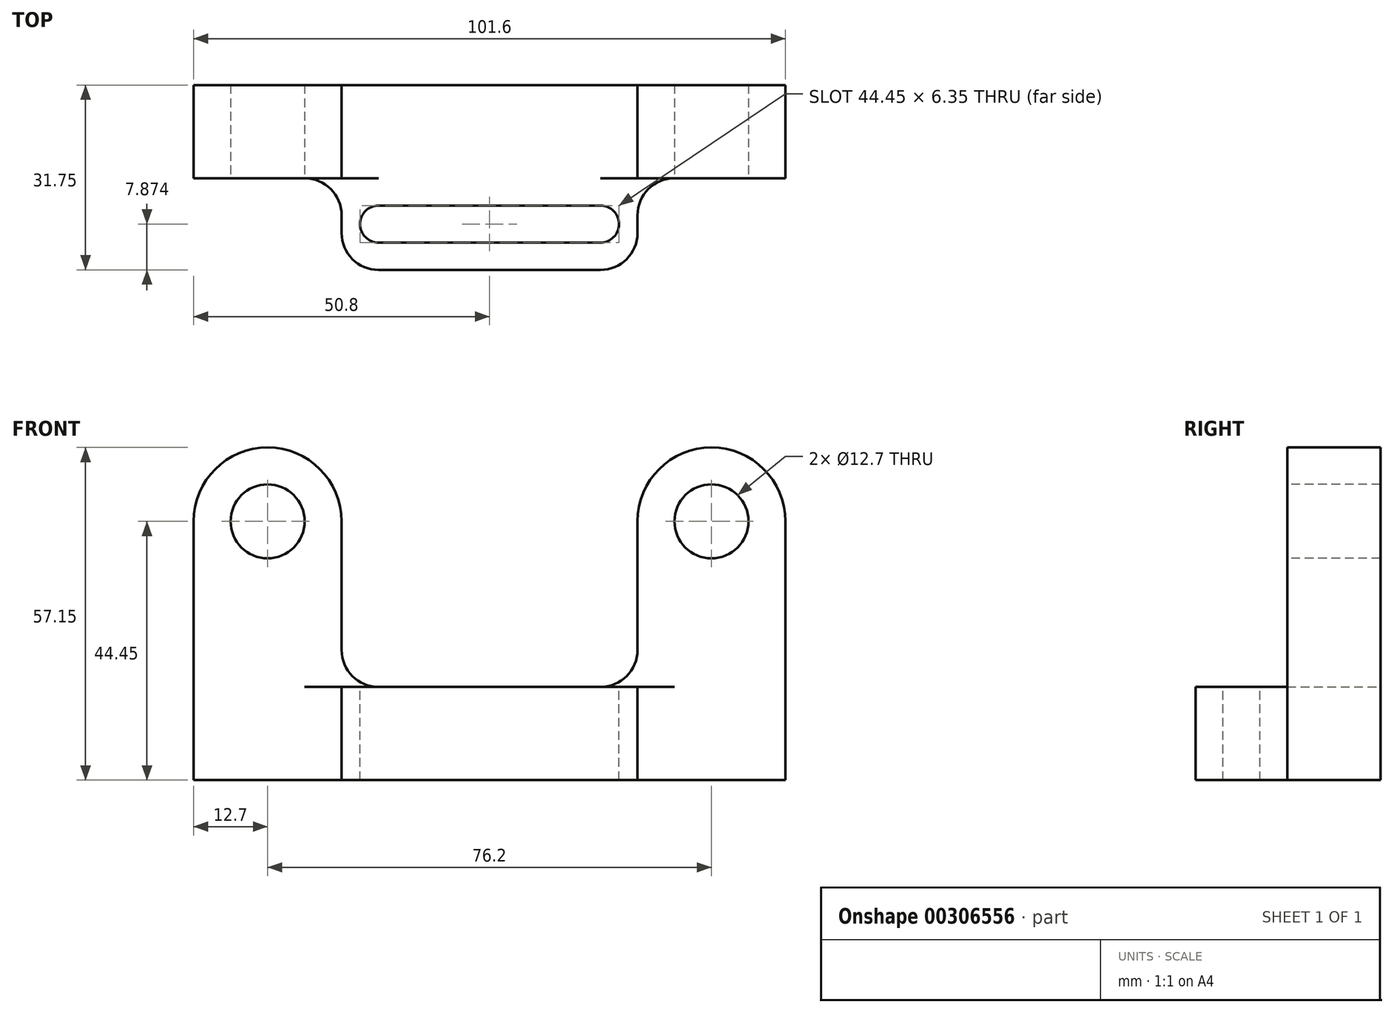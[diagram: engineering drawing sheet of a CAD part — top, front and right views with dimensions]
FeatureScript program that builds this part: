
annotation { "Feature Type Name" : "Feature", "Feature Type Description" : "" }
export const myFeature = defineFeature(function(context is Context, id is Id, definition is map)
    precondition{}
    {
        {
            var Q0;
            Q0=qCreatedBy(makeId("Front.planeOp"),FACE);
            var sketch = newSketch(context, id + "F0", { "sketchPlane" : qUnion([Q0])});
            skLineSegment(sketch, "E0", {"start": v(0, 0) * mm, "end": v(50.8, 0) * mm});
            skLineSegment(sketch, "E1", {"start": v(50.8, 0) * mm, "end": v(50.8, 44.45) * mm});
            skLineSegment(sketch, "E2", {"start": v(0, 0) * mm, "end": v(0, 16) * mm});
            skLineSegment(sketch, "E3", {"start": v(0, 16) * mm, "end": v(19.05, 16) * mm});
            skLineSegment(sketch, "E4", {"start": v(25.4, 22.35) * mm, "end": v(25.4, 44.45) * mm});
            skArc(sketch, "E5", {"start": v(50.8, 44.45) * mm, "mid": v(38.1, 57.15) * mm, "end": v(25.4, 44.45) * mm});
            skPoint(sketch, "E6.visualSharp", {"position": v(25.4, 16) * mm});
            skArc(sketch, "E6.filletArc", {"start": v(19.05, 16) * mm, "mid": v(23.54, 17.86) * mm, "end": v(25.4, 22.35) * mm});
            skLineSegment(sketch, "E7", {"start": v(0, 16) * mm, "end": v(-19.05, 16) * mm});
            skLineSegment(sketch, "E8", {"start": v(-25.4, 22.35) * mm, "end": v(-25.4, 44.45) * mm});
            skLineSegment(sketch, "E9", {"start": v(-50.8, 44.45) * mm, "end": v(-50.8, 0) * mm});
            skLineSegment(sketch, "E10", {"start": v(-50.8, 0) * mm, "end": v(0, 0) * mm});
            skArc(sketch, "E11", {"start": v(-25.4, 44.45) * mm, "mid": v(-38.1, 57.15) * mm, "end": v(-50.8, 44.45) * mm});
            skPoint(sketch, "E12.visualSharp", {"position": v(-25.4, 16) * mm});
            skArc(sketch, "E12.filletArc", {"start": v(-25.4, 22.35) * mm, "mid": v(-23.54, 17.86) * mm, "end": v(-19.05, 16) * mm});
            skSolve(sketch);
        }
        {
            var Q0;
            Q0=makeQuery(id+"F0.imprint","IMPRINT",FACE,{"disambiguationData":[TD([[makeQuery(id+"F0.imprint","IMPRINT",EDGE,{"derivedFrom":sQuery(id+"F0.wireOp",EDGE,"E2")}),1.0]])]});
            var Q1;
            Q1=makeQuery(id+"F0.imprint","IMPRINT",FACE,{"disambiguationData":[TD([[makeQuery(id+"F0.imprint","IMPRINT",EDGE,{"derivedFrom":sQuery(id+"F0.wireOp",EDGE,"E0")}),1.0]])]});
            extrude(context, id + "F1", {"entities" : qUnion([Q0, Q1]), "depth" : 31.75 * mm});
        }
        {
            var Q0;
            Q0=makeQuery(id+"F1.opExtrude","SWEPT_FACE",FACE,{"disambiguationData":[OSD([sQuery(id+"F0.wireOp",EDGE,"E1")])]});
            var sketch = newSketch(context, id + "F2", { "sketchPlane" : qUnion([Q0])});
            skLineSegment(sketch, "E13", {"start": v(0, 0) * mm, "end": v(-16, 0) * mm});
            skLineSegment(sketch, "E14", {"start": v(-16, 0) * mm, "end": v(-16, 57.15) * mm});
            skLineSegment(sketch, "E15", {"start": v(-16, 57.15) * mm, "end": v(0, 57.15) * mm});
            skLineSegment(sketch, "E16", {"start": v(0, 57.15) * mm, "end": v(0, 0) * mm});
            skLineSegment(sketch, "E17", {"start": v(-16, 0) * mm, "end": v(-31.75, 0) * mm});
            skLineSegment(sketch, "E18", {"start": v(-31.75, 0) * mm, "end": v(-31.75, 57.15) * mm});
            skLineSegment(sketch, "E19", {"start": v(-31.75, 57.15) * mm, "end": v(-16, 57.15) * mm});
            skLineSegment(sketch, "E20", {"start": v(-31.75, 16) * mm, "end": v(-16, 16) * mm});
            skSolve(sketch);
        }
        {
            var Q0;
            {var subQ0=sQuery(id+"F2.wireOp",EDGE,"E20");Q0=makeQuery(id+"F2.imprint","IMPRINT",FACE,{"disambiguationData":[TD([[makeQuery(id+"F2.imprint","IMPRINT",EDGE,{"derivedFrom":subQ0}),1.0]])]});}
            var Q1;
            {var subQ0=sQuery(id+"F2.wireOp",EDGE,"E19");Q1=makeQuery(id+"F2.imprint","IMPRINT",FACE,{"disambiguationData":[TD([[makeQuery(id+"F2.imprint","IMPRINT",EDGE,{"derivedFrom":subQ0}),-1.0]])]});}
            extrude(context, id + "F3", {"entities" : qUnion([Q0, Q1]), "operationType" : NewBodyOperationType.REMOVE, "endBound" : BoundingType.THROUGH_ALL, "oppositeDirection" : true, "depth" : 25.4 * mm});
        }
        {
            var Q0;
            Q0=makeQuery(id+"F3.boolean.opBoolean","MERGE",FACE,{"derivedFrom":[makeQuery(id+"F1.opExtrude","SWEPT_FACE",FACE,{"disambiguationData":[OSD([sQuery(id+"F0.wireOp",EDGE,"E3"),sQuery(id+"F0.wireOp",EDGE,"E7")])]}),makeQuery(id+"F3.opExtrude","SWEPT_FACE",FACE,{"disambiguationData":[OSD([sQuery(id+"F2.wireOp",EDGE,"E20")])]})]});
            var sketch = newSketch(context, id + "F4", { "sketchPlane" : qUnion([Q0])});
            skLineSegment(sketch, "E21", {"start": v(-50.8, -16) * mm, "end": v(-31.75, -16) * mm});
            skLineSegment(sketch, "E22", {"start": v(31.75, -16) * mm, "end": v(50.8, -16) * mm});
            skLineSegment(sketch, "E23", {"start": v(50.8, -23.88) * mm, "end": v(19.05, -23.88) * mm, "construction": true});
            skLineSegment(sketch, "E24", {"start": v(19.05, -23.88) * mm, "end": v(-19.05, -23.88) * mm, "construction": true});
            skLineSegment(sketch, "E25", {"start": v(-19.05, -23.88) * mm, "end": v(-50.8, -23.88) * mm, "construction": true});
            skCircle(sketch, "E26", {"center": v(-19.05, -23.88) * mm, "radius": 3.18 * mm});
            skCircle(sketch, "E27", {"center": v(19.05, -23.88) * mm, "radius": 3.18 * mm});
            skLineSegment(sketch, "E28", {"start": v(-19.05, -20.7) * mm, "end": v(19.05, -20.7) * mm});
            skLineSegment(sketch, "E29", {"start": v(19.05, -20.7) * mm, "end": v(19.05, -27.05) * mm});
            skLineSegment(sketch, "E30", {"start": v(19.05, -27.05) * mm, "end": v(-19.05, -27.05) * mm});
            skLineSegment(sketch, "E31", {"start": v(-25.4, -22.35) * mm, "end": v(-25.4, -25.4) * mm});
            skLineSegment(sketch, "E32", {"start": v(-19.05, -31.75) * mm, "end": v(19.05, -31.75) * mm});
            skLineSegment(sketch, "E33", {"start": v(25.4, -25.4) * mm, "end": v(25.4, -22.35) * mm});
            skLineSegment(sketch, "E34", {"start": v(28.25, -16) * mm, "end": v(50.8, -16) * mm});
            skPoint(sketch, "E35.visualSharp", {"position": v(-25.4, -16) * mm});
            skArc(sketch, "E35.filletArc", {"start": v(-25.4, -22.35) * mm, "mid": v(-27.26, -17.86) * mm, "end": v(-31.75, -16) * mm});
            skPoint(sketch, "E36.visualSharp", {"position": v(-25.4, -31.75) * mm});
            skArc(sketch, "E36.filletArc", {"start": v(-25.4, -25.4) * mm, "mid": v(-23.54, -29.9) * mm, "end": v(-19.05, -31.75) * mm});
            skArc(sketch, "E37.filletArc", {"start": v(31.75, -16) * mm, "mid": v(27.26, -17.86) * mm, "end": v(25.4, -22.35) * mm});
            skPoint(sketch, "E38.visualSharp", {"position": v(25.4, -31.75) * mm});
            skArc(sketch, "E38.filletArc", {"start": v(19.05, -31.75) * mm, "mid": v(23.54, -29.9) * mm, "end": v(25.4, -25.4) * mm});
            skSolve(sketch);
        }
        {
            var Q0;
            Q0=makeQuery(id+"F4.imprint","IMPRINT",FACE,{"disambiguationData":[TD([[makeQuery(id+"F4.imprint","IMPRINT",EDGE,{"derivedFrom":sQuery(id+"F4.wireOp",EDGE,"E21")}),-1.0]])]});
            var Q1;
            {var subQ0=sQuery(id+"F4.wireOp",EDGE,"E28");Q1=makeQuery(id+"F4.imprint","IMPRINT",FACE,{"disambiguationData":[TD([[makeQuery(id+"F4.imprint","IMPRINT",EDGE,{"derivedFrom":subQ0}),-1.0]])]});}
            var Q2;
            {var subQ0=sQuery(id+"F4.wireOp",EDGE,"E26");var subQ1=makeQuery(id+"F4.imprint","INTERSECT",VERTEX,{"derivedFrom":[subQ0,sQuery(id+"F4.wireOp",EDGE,"E28")]});Q2=makeQuery(id+"F4.imprint","IMPRINT",FACE,{"disambiguationData":[TD([[makeQuery(id+"F4.imprint","IMPRINT",EDGE,{"disambiguationData":[TD([[subQ1,-1.0]])],"derivedFrom":subQ0}),1.0]])]});}
            var Q3;
            {var subQ0=sQuery(id+"F4.wireOp",EDGE,"E29");Q3=makeQuery(id+"F4.imprint","IMPRINT",FACE,{"disambiguationData":[TD([[makeQuery(id+"F4.imprint","IMPRINT",EDGE,{"derivedFrom":subQ0}),1.0]])]});}
            var Q4;
            {var subQ0=sQuery(id+"F4.wireOp",EDGE,"E29");Q4=makeQuery(id+"F4.imprint","IMPRINT",FACE,{"disambiguationData":[TD([[makeQuery(id+"F4.imprint","IMPRINT",EDGE,{"derivedFrom":subQ0}),-1.0]])]});}
            var Q5;
            Q5=makeQuery(id+"F4.imprint","IMPRINT",FACE,{"disambiguationData":[TD([[makeQuery(id+"F4.imprint","IMPRINT",EDGE,{"derivedFrom":sQuery(id+"F4.wireOp",EDGE,"E33")}),-1.0]])]});
            extrude(context, id + "F5", {"entities" : qUnion([Q0, Q1, Q2, Q3, Q4, Q5]), "operationType" : NewBodyOperationType.REMOVE, "endBound" : BoundingType.THROUGH_ALL, "oppositeDirection" : true, "depth" : 25.4 * mm});
        }
        {
            var Q0;
            Q0=makeQuery(id+"F5.boolean.opBoolean","MERGE",FACE,{"derivedFrom":[makeQuery(id+"F3.boolean.opBoolean","COPY",FACE,{"disambiguationData":[TD([makeQuery(id+"F1.opExtrude","SWEPT_FACE",FACE,{"disambiguationData":[OSD([sQuery(id+"F0.wireOp",EDGE,"E8")])]})])],"derivedFrom":makeQuery(id+"F3.opExtrude","SWEPT_FACE",FACE,{"disambiguationData":[OSD([sQuery(id+"F2.wireOp",EDGE,"E14")])]})}),makeQuery(id+"F5.opExtrude","SWEPT_FACE",FACE,{"disambiguationData":[OSD([sQuery(id+"F4.wireOp",EDGE,"E21")])]})]});
            var sketch = newSketch(context, id + "F6", { "sketchPlane" : qUnion([Q0])});
            skCircle(sketch, "E39", {"center": v(-38.1, 44.45) * mm, "radius": 6.35 * mm});
            skSolve(sketch);
        }
        {
            var Q0;
            Q0=makeQuery(id+"F6.imprint","IMPRINT",FACE,{"disambiguationData":[TD([[makeQuery(id+"F6.imprint","IMPRINT",EDGE,{"derivedFrom":sQuery(id+"F6.wireOp",EDGE,"E39")}),1.0]])]});
            extrude(context, id + "F7", {"entities" : qUnion([Q0]), "operationType" : NewBodyOperationType.REMOVE, "endBound" : BoundingType.THROUGH_ALL, "oppositeDirection" : true, "depth" : 25.4 * mm});
        }
        {
            var Q0;
            Q0=makeQuery(id+"F5.boolean.opBoolean","MERGE",FACE,{"derivedFrom":[makeQuery(id+"F3.boolean.opBoolean","COPY",FACE,{"disambiguationData":[TD([makeQuery(id+"F1.opExtrude","SWEPT_FACE",FACE,{"disambiguationData":[OSD([sQuery(id+"F0.wireOp",EDGE,"E1")])]})])],"derivedFrom":makeQuery(id+"F3.opExtrude","SWEPT_FACE",FACE,{"disambiguationData":[OSD([sQuery(id+"F2.wireOp",EDGE,"E14")])]})}),makeQuery(id+"F5.opExtrude","SWEPT_FACE",FACE,{"disambiguationData":[OSD([sQuery(id+"F4.wireOp",EDGE,"E34")])]})]});
            var sketch = newSketch(context, id + "F8", { "sketchPlane" : qUnion([Q0])});
            skCircle(sketch, "E40", {"center": v(38.1, 44.45) * mm, "radius": 6.35 * mm});
            skSolve(sketch);
        }
        {
            var Q0;
            Q0=makeQuery(id+"F8.imprint","IMPRINT",FACE,{"disambiguationData":[TD([[makeQuery(id+"F8.imprint","IMPRINT",EDGE,{"derivedFrom":sQuery(id+"F8.wireOp",EDGE,"E40")}),1.0]])]});
            extrude(context, id + "F9", {"entities" : qUnion([Q0]), "operationType" : NewBodyOperationType.REMOVE, "endBound" : BoundingType.THROUGH_ALL, "oppositeDirection" : true, "depth" : 25.4 * mm});
        }
    });
